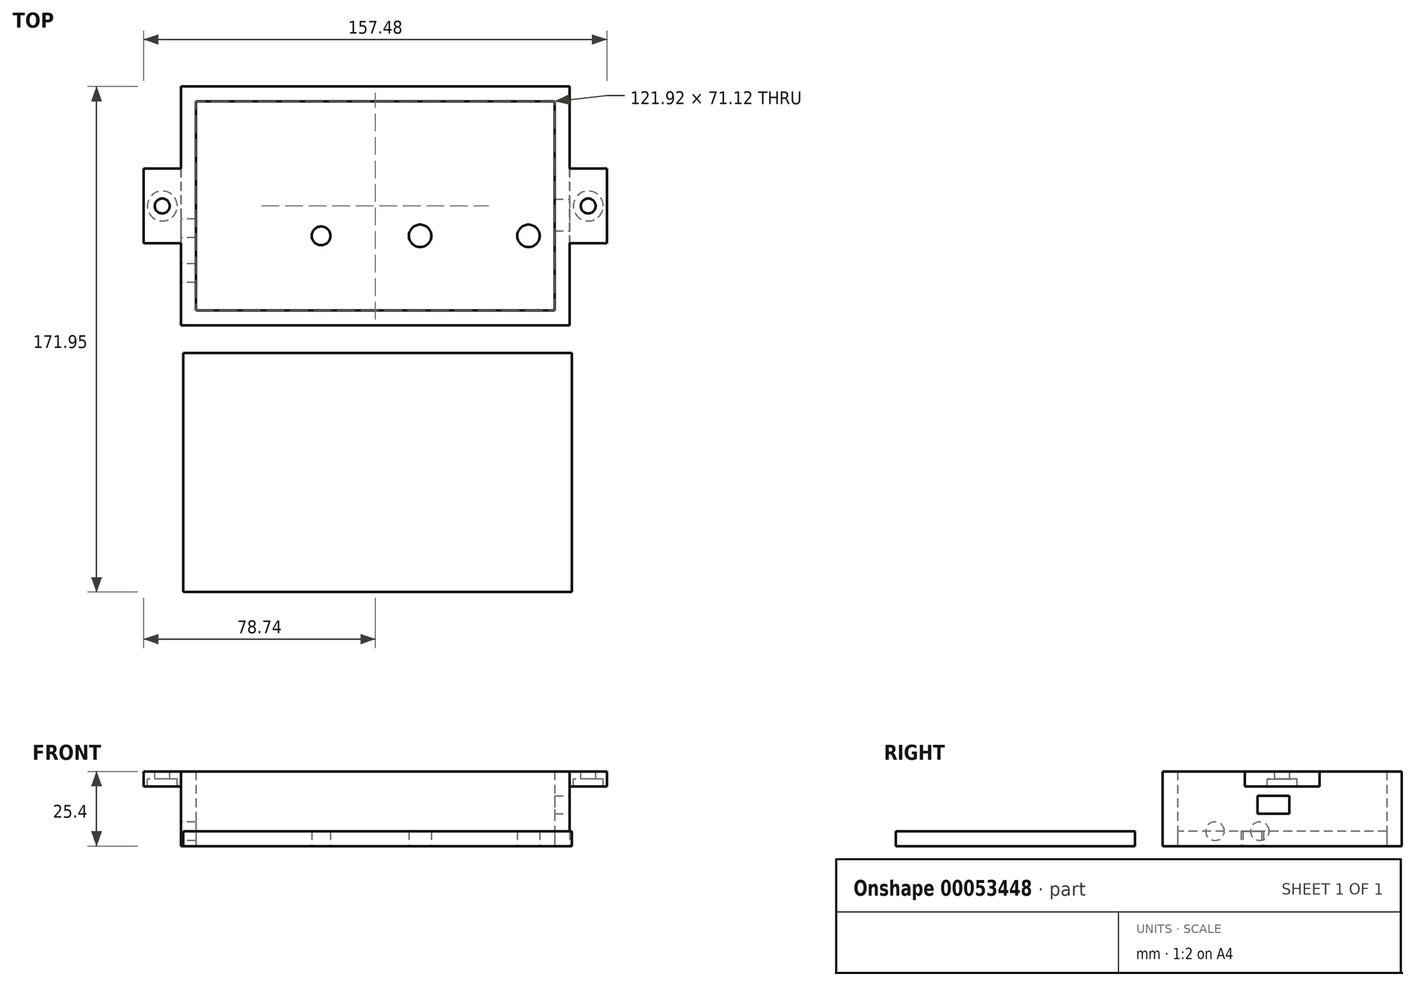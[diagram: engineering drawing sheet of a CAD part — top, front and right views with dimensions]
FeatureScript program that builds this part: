
annotation { "Feature Type Name" : "Feature", "Feature Type Description" : "" }
export const myFeature = defineFeature(function(context is Context, id is Id, definition is map)
    precondition{}
    {
        {
            var Q0;
            Q0=qCreatedBy(makeId("Top.planeOp"),FACE);
            var sketch = newSketch(context, id + "F0", { "sketchPlane" : qUnion([Q0])});
            skLineSegment(sketch, "E0.bottom", {"start": v(-121.92, 71.12) * mm, "end": v(0, 71.12) * mm});
            skLineSegment(sketch, "E0.top", {"start": v(-121.92, 0) * mm, "end": v(0, 0) * mm});
            skLineSegment(sketch, "E0.left", {"start": v(-121.92, 71.12) * mm, "end": v(-121.92, 0) * mm});
            skLineSegment(sketch, "E0.right", {"start": v(0, 71.12) * mm, "end": v(0, 0) * mm});
            skSolve(sketch);
        }
        {
            var Q0;
            Q0=makeQuery(id+"F0.imprint","IMPRINT",FACE,{"disambiguationData":[TD([[makeQuery(id+"F0.imprint","IMPRINT",EDGE,{"derivedFrom":sQuery(id+"F0.wireOp",EDGE,"E0.bottom")}),-1.0]])]});
            extrude(context, id + "F1", {"entities" : qUnion([Q0]), "depth" : 5.08 * mm});
        }
        {
            var Q0;
            Q0=makeQuery(id+"F1.opExtrude","CAP_FACE",FACE,{"disambiguationData":[OSD([sQuery(id+"F0.wireOp",EDGE,"E0.bottom"),sQuery(id+"F0.wireOp",EDGE,"E0.top"),sQuery(id+"F0.wireOp",EDGE,"E0.left"),sQuery(id+"F0.wireOp",EDGE,"E0.right")])],"isStart":true});
            var sketch = newSketch(context, id + "F2", { "sketchPlane" : qUnion([Q0])});
            skLineSegment(sketch, "E1.bottom", {"start": v(5.08, 5.08) * mm, "end": v(-127, 5.08) * mm});
            skLineSegment(sketch, "E1.top", {"start": v(5.08, -76.2) * mm, "end": v(-127, -76.2) * mm});
            skLineSegment(sketch, "E1.left", {"start": v(5.08, 5.08) * mm, "end": v(5.08, -76.2) * mm});
            skLineSegment(sketch, "E1.right", {"start": v(-127, 5.08) * mm, "end": v(-127, -76.2) * mm});
            skSolve(sketch);
        }
        {
            var Q0;
            {var subQ0=sQuery(id+"F2.wireOp",EDGE,"E1.top");Q0=makeQuery(id+"F2.imprint","IMPRINT",FACE,{"disambiguationData":[TD([[makeQuery(id+"F2.imprint","IMPRINT",EDGE,{"derivedFrom":subQ0}),-1.0]])]});}
            extrude(context, id + "F3", {"entities" : qUnion([Q0]), "oppositeDirection" : true, "depth" : 25.4 * mm});
        }
        {
            var Q0;
            Q0=makeQuery(id+"F1.opExtrude","CAP_FACE",FACE,{"disambiguationData":[OSD([sQuery(id+"F0.wireOp",EDGE,"E0.bottom"),sQuery(id+"F0.wireOp",EDGE,"E0.top"),sQuery(id+"F0.wireOp",EDGE,"E0.left"),sQuery(id+"F0.wireOp",EDGE,"E0.right")])],"isStart":true});
            var sketch = newSketch(context, id + "F4", { "sketchPlane" : qUnion([Q0])});
            skCircle(sketch, "E2", {"center": v(-45.72, -25.4) * mm, "radius": 3.8 * mm});
            skSolve(sketch);
        }
        {
            var Q0;
            Q0=makeQuery(id+"F4.imprint","IMPRINT",FACE,{"disambiguationData":[TD([[makeQuery(id+"F4.imprint","IMPRINT",EDGE,{"derivedFrom":sQuery(id+"F4.wireOp",EDGE,"E2")}),1.0]])]});
            extrude(context, id + "F5", {"entities" : qUnion([Q0]), "operationType" : NewBodyOperationType.REMOVE, "oppositeDirection" : true, "depth" : 5.08 * mm});
        }
        {
            var Q0;
            Q0=makeQuery(id+"F1.opExtrude","CAP_FACE",FACE,{"disambiguationData":[OSD([sQuery(id+"F0.wireOp",EDGE,"E0.bottom"),sQuery(id+"F0.wireOp",EDGE,"E0.top"),sQuery(id+"F0.wireOp",EDGE,"E0.left"),sQuery(id+"F0.wireOp",EDGE,"E0.right")])],"isStart":true});
            var sketch = newSketch(context, id + "F6", { "sketchPlane" : qUnion([Q0])});
            skCircle(sketch, "E3", {"center": v(-8.9, -25.4) * mm, "radius": 3.81 * mm});
            skSolve(sketch);
        }
        {
            var Q0;
            Q0=makeQuery(id+"F6.imprint","IMPRINT",FACE,{"disambiguationData":[TD([[makeQuery(id+"F6.imprint","IMPRINT",EDGE,{"derivedFrom":sQuery(id+"F6.wireOp",EDGE,"E3")}),1.0]])]});
            extrude(context, id + "F7", {"entities" : qUnion([Q0]), "operationType" : NewBodyOperationType.REMOVE, "oppositeDirection" : true, "depth" : 5.08 * mm});
        }
        {
            var Q0;
            Q0=makeQuery(id+"F1.opExtrude","CAP_FACE",FACE,{"disambiguationData":[OSD([sQuery(id+"F0.wireOp",EDGE,"E0.bottom"),sQuery(id+"F0.wireOp",EDGE,"E0.top"),sQuery(id+"F0.wireOp",EDGE,"E0.left"),sQuery(id+"F0.wireOp",EDGE,"E0.right")])],"isStart":true});
            var sketch = newSketch(context, id + "F8", { "sketchPlane" : qUnion([Q0])});
            skCircle(sketch, "E4", {"center": v(-79.38, -25.4) * mm, "radius": 3.18 * mm});
            skSolve(sketch);
        }
        {
            var Q0;
            Q0=makeQuery(id+"F8.imprint","IMPRINT",FACE,{"disambiguationData":[TD([[makeQuery(id+"F8.imprint","IMPRINT",EDGE,{"derivedFrom":sQuery(id+"F8.wireOp",EDGE,"E4")}),1.0]])]});
            extrude(context, id + "F9", {"entities" : qUnion([Q0]), "operationType" : NewBodyOperationType.REMOVE, "oppositeDirection" : true, "depth" : 5.08 * mm});
        }
        {
            var Q0;
            Q0=makeQuery(id+"F3.opExtrude","SWEPT_FACE",FACE,{"disambiguationData":[OSD([sQuery(id+"F2.wireOp",EDGE,"E1.right")])]});
            var sketch = newSketch(context, id + "F10", { "sketchPlane" : qUnion([Q0])});
            skCircle(sketch, "E5", {"center": v(-27.94, 5.08) * mm, "radius": 3.18 * mm});
            skSolve(sketch);
        }
        {
            var Q0;
            Q0=makeQuery(id+"F10.imprint","IMPRINT",FACE,{"disambiguationData":[TD([[makeQuery(id+"F10.imprint","IMPRINT",EDGE,{"derivedFrom":sQuery(id+"F10.wireOp",EDGE,"E5")}),-1.0]])]});
            var sketch = newSketch(context, id + "F11", { "sketchPlane" : qUnion([Q0])});
            skCircle(sketch, "E6", {"center": v(-12.7, 5.08) * mm, "radius": 3.18 * mm});
            skSolve(sketch);
        }
        {
            var Q0;
            Q0=makeQuery(id+"F11.imprint","IMPRINT",FACE,{"disambiguationData":[TD([[makeQuery(id+"F11.imprint","IMPRINT",EDGE,{"derivedFrom":makeQuery(id+"F10.imprint","IMPRINT",EDGE,{"derivedFrom":sQuery(id+"F10.wireOp",EDGE,"E5")})}),1.0]])]});
            extrude(context, id + "F12", {"entities" : qUnion([Q0]), "operationType" : NewBodyOperationType.REMOVE, "oppositeDirection" : true, "depth" : 5.08 * mm});
        }
        {
            var Q0;
            Q0 = qSketchRegion(id + "F11", true);
            extrude(context, id + "F13", {"entities" : qUnion([Q0]), "operationType" : NewBodyOperationType.REMOVE, "oppositeDirection" : true, "depth" : 5.08 * mm});
        }
        {
            var Q0;
            Q0=makeQuery(id+"F3.opExtrude","SWEPT_FACE",FACE,{"disambiguationData":[OSD([sQuery(id+"F2.wireOp",EDGE,"E1.left")])]});
            var sketch = newSketch(context, id + "F14", { "sketchPlane" : qUnion([Q0])});
            skLineSegment(sketch, "E7.bottom", {"start": v(37.94, 17.1) * mm, "end": v(27.12, 17.1) * mm});
            skLineSegment(sketch, "E7.top", {"start": v(37.94, 11) * mm, "end": v(27.12, 11) * mm});
            skLineSegment(sketch, "E7.left", {"start": v(37.94, 17.1) * mm, "end": v(37.94, 11) * mm});
            skLineSegment(sketch, "E7.right", {"start": v(27.12, 17.1) * mm, "end": v(27.12, 11) * mm});
            skSolve(sketch);
        }
        {
            var Q0;
            Q0 = qSketchRegion(id + "F14", true);
            extrude(context, id + "F15", {"entities" : qUnion([Q0]), "operationType" : NewBodyOperationType.REMOVE, "oppositeDirection" : true, "depth" : 5.08 * mm});
        }
        {
            var Q0;
            Q0=makeQuery(id+"F3.opExtrude","SWEPT_FACE",FACE,{"disambiguationData":[OSD([sQuery(id+"F2.wireOp",EDGE,"E1.left")])]});
            var sketch = newSketch(context, id + "F16", { "sketchPlane" : qUnion([Q0])});
            skLineSegment(sketch, "E8.bottom", {"start": v(48.26, 25.4) * mm, "end": v(22.86, 25.4) * mm});
            skLineSegment(sketch, "E8.top", {"start": v(48.26, 20.32) * mm, "end": v(22.86, 20.32) * mm});
            skLineSegment(sketch, "E8.left", {"start": v(48.26, 25.4) * mm, "end": v(48.26, 20.32) * mm});
            skLineSegment(sketch, "E8.right", {"start": v(22.86, 25.4) * mm, "end": v(22.86, 20.32) * mm});
            skSolve(sketch);
        }
        {
            var Q0;
            Q0=makeQuery(id+"F16.imprint","IMPRINT",FACE,{"disambiguationData":[TD([[makeQuery(id+"F16.imprint","IMPRINT",EDGE,{"derivedFrom":sQuery(id+"F16.wireOp",EDGE,"E8.bottom")}),-1.0]])]});
            extrude(context, id + "F17", {"entities" : qUnion([Q0]), "operationType" : NewBodyOperationType.ADD, "depth" : 12.7 * mm});
        }
        {
            var Q0;
            Q0=makeQuery(id+"F10.imprint","IMPRINT",FACE,{"disambiguationData":[TD([[makeQuery(id+"F10.imprint","IMPRINT",EDGE,{"derivedFrom":sQuery(id+"F10.wireOp",EDGE,"E5")}),-1.0]])]});
            var sketch = newSketch(context, id + "F18", { "sketchPlane" : qUnion([Q0])});
            skLineSegment(sketch, "E9.bottom", {"start": v(-48.26, 25.4) * mm, "end": v(-22.86, 25.4) * mm});
            skLineSegment(sketch, "E9.top", {"start": v(-48.26, 20.32) * mm, "end": v(-22.86, 20.32) * mm});
            skLineSegment(sketch, "E9.left", {"start": v(-48.26, 25.4) * mm, "end": v(-48.26, 20.32) * mm});
            skLineSegment(sketch, "E9.right", {"start": v(-22.86, 25.4) * mm, "end": v(-22.86, 20.32) * mm});
            skSolve(sketch);
        }
        {
            var Q0;
            Q0 = qSketchRegion(id + "F18", true);
            extrude(context, id + "F19", {"entities" : qUnion([Q0]), "operationType" : NewBodyOperationType.ADD, "depth" : 12.7 * mm});
        }
        {
            var Q0;
            Q0=makeQuery(id+"F19.boolean.opBoolean","MERGE",FACE,{"derivedFrom":[makeQuery(id+"F17.boolean.opBoolean","MERGE",FACE,{"derivedFrom":[makeQuery(id+"F3.opExtrude","CAP_FACE",FACE,{"disambiguationData":[OSD([sQuery(id+"F0.wireOp",EDGE,"E0.bottom"),sQuery(id+"F0.wireOp",EDGE,"E0.top"),sQuery(id+"F0.wireOp",EDGE,"E0.left"),sQuery(id+"F0.wireOp",EDGE,"E0.right"),sQuery(id+"F2.wireOp",EDGE,"E1.bottom"),sQuery(id+"F2.wireOp",EDGE,"E1.top"),sQuery(id+"F2.wireOp",EDGE,"E1.left"),sQuery(id+"F2.wireOp",EDGE,"E1.right")])],"isStart":false}),makeQuery(id+"F17.opExtrude","SWEPT_FACE",FACE,{"disambiguationData":[OSD([sQuery(id+"F16.wireOp",EDGE,"E8.bottom")])]})]}),makeQuery(id+"F19.opExtrude","SWEPT_FACE",FACE,{"disambiguationData":[OSD([sQuery(id+"F18.wireOp",EDGE,"E9.bottom")])]})]});
            var sketch = newSketch(context, id + "F20", { "sketchPlane" : qUnion([Q0])});
            skCircle(sketch, "E10", {"center": v(11.43, 35.56) * mm, "radius": 5.08 * mm});
            skSolve(sketch);
        }
        {
            var Q0;
            Q0 = qSketchRegion(id + "F20", true);
            extrude(context, id + "F21", {"entities" : qUnion([Q0]), "operationType" : NewBodyOperationType.REMOVE, "oppositeDirection" : true, "depth" : 5.08 * mm});
        }
        {
            var Q0;
            Q0=makeQuery(id+"F19.boolean.opBoolean","MERGE",FACE,{"derivedFrom":[makeQuery(id+"F17.boolean.opBoolean","MERGE",FACE,{"derivedFrom":[makeQuery(id+"F3.opExtrude","CAP_FACE",FACE,{"disambiguationData":[OSD([sQuery(id+"F0.wireOp",EDGE,"E0.bottom"),sQuery(id+"F0.wireOp",EDGE,"E0.top"),sQuery(id+"F0.wireOp",EDGE,"E0.left"),sQuery(id+"F0.wireOp",EDGE,"E0.right"),sQuery(id+"F2.wireOp",EDGE,"E1.bottom"),sQuery(id+"F2.wireOp",EDGE,"E1.top"),sQuery(id+"F2.wireOp",EDGE,"E1.left"),sQuery(id+"F2.wireOp",EDGE,"E1.right")])],"isStart":false}),makeQuery(id+"F17.opExtrude","SWEPT_FACE",FACE,{"disambiguationData":[OSD([sQuery(id+"F16.wireOp",EDGE,"E8.bottom")])]})]}),makeQuery(id+"F19.opExtrude","SWEPT_FACE",FACE,{"disambiguationData":[OSD([sQuery(id+"F18.wireOp",EDGE,"E9.bottom")])]})]});
            var sketch = newSketch(context, id + "F22", { "sketchPlane" : qUnion([Q0])});
            skCircle(sketch, "E11", {"center": v(-133.35, 35.56) * mm, "radius": 5.08 * mm});
            skSolve(sketch);
        }
        {
            var Q0;
            Q0 = qSketchRegion(id + "F22", true);
            extrude(context, id + "F23", {"entities" : qUnion([Q0]), "operationType" : NewBodyOperationType.REMOVE, "oppositeDirection" : true, "depth" : 5.08 * mm});
        }
        {
            var Q0;
            Q0=qCreatedBy(makeId("Top.planeOp"),FACE);
            var sketch = newSketch(context, id + "F24", { "sketchPlane" : qUnion([Q0])});
            skLineSegment(sketch, "E12.bottom", {"start": v(5.86, -14.47) * mm, "end": v(-126.22, -14.47) * mm});
            skLineSegment(sketch, "E12.top", {"start": v(5.86, -95.75) * mm, "end": v(-126.22, -95.75) * mm});
            skLineSegment(sketch, "E12.left", {"start": v(5.86, -14.47) * mm, "end": v(5.86, -95.75) * mm});
            skLineSegment(sketch, "E12.right", {"start": v(-126.22, -14.47) * mm, "end": v(-126.22, -95.75) * mm});
            skSolve(sketch);
        }
        {
            var Q0;
            Q0=makeQuery(id+"F24.imprint","IMPRINT",FACE,{"disambiguationData":[TD([[makeQuery(id+"F24.imprint","IMPRINT",EDGE,{"derivedFrom":sQuery(id+"F24.wireOp",EDGE,"E12.bottom")}),1.0]])]});
            extrude(context, id + "F25", {"entities" : qUnion([Q0]), "depth" : 5.08 * mm});
        }
        {
            var Q0;
            Q0=makeQuery(id+"F19.boolean.opBoolean","MERGE",FACE,{"derivedFrom":[makeQuery(id+"F17.boolean.opBoolean","MERGE",FACE,{"derivedFrom":[makeQuery(id+"F3.opExtrude","CAP_FACE",FACE,{"disambiguationData":[OSD([sQuery(id+"F0.wireOp",EDGE,"E0.bottom"),sQuery(id+"F0.wireOp",EDGE,"E0.top"),sQuery(id+"F0.wireOp",EDGE,"E0.left"),sQuery(id+"F0.wireOp",EDGE,"E0.right"),sQuery(id+"F2.wireOp",EDGE,"E1.bottom"),sQuery(id+"F2.wireOp",EDGE,"E1.top"),sQuery(id+"F2.wireOp",EDGE,"E1.left"),sQuery(id+"F2.wireOp",EDGE,"E1.right")])],"isStart":false}),makeQuery(id+"F17.opExtrude","SWEPT_FACE",FACE,{"disambiguationData":[OSD([sQuery(id+"F16.wireOp",EDGE,"E8.bottom")])]})]}),makeQuery(id+"F19.opExtrude","SWEPT_FACE",FACE,{"disambiguationData":[OSD([sQuery(id+"F18.wireOp",EDGE,"E9.bottom")])]})]});
            var sketch = newSketch(context, id + "F26", { "sketchPlane" : qUnion([Q0])});
            skCircle(sketch, "E13.0", {"center": v(11.43, 35.56) * mm, "radius": 5.08 * mm});
            skLineSegment(sketch, "E14", {"start": v(11.43, 35.56) * mm, "end": v(8.9, 35.56) * mm});
            skLineSegment(sketch, "E15", {"start": v(8.9, 35.56) * mm, "end": v(6.35, 35.56) * mm});
            skCircle(sketch, "E16", {"center": v(11.43, 35.56) * mm, "radius": 2.54 * mm});
            skLineSegment(sketch, "E17.1", {"start": v(5.08, -5.08) * mm, "end": v(-127, -5.08) * mm});
            skLineSegment(sketch, "E18", {"start": v(-60.96, -5.08) * mm, "end": v(-60.96, 76.2) * mm, "construction": true});
            skCircle(sketch, "E19.MirrorC", {"center": v(-133.35, 35.56) * mm, "radius": 5.08 * mm});
            skCircle(sketch, "E20.MirrorC", {"center": v(-133.35, 35.56) * mm, "radius": 2.54 * mm});
            skSolve(sketch);
        }
        {
            var Q0;
            Q0=makeQuery(id+"F26.imprint","IMPRINT",FACE,{"disambiguationData":[TD([[makeQuery(id+"F26.imprint","IMPRINT",EDGE,{"derivedFrom":sQuery(id+"F26.wireOp",EDGE,"E13.0")}),1.0]])]});
            var Q1;
            Q1=makeQuery(id+"F26.imprint","IMPRINT",FACE,{"disambiguationData":[TD([[makeQuery(id+"F26.imprint","IMPRINT",EDGE,{"derivedFrom":sQuery(id+"F26.wireOp",EDGE,"E19.MirrorC")}),1.0]])]});
            extrude(context, id + "F27", {"entities" : qUnion([Q0, Q1]), "operationType" : NewBodyOperationType.ADD, "oppositeDirection" : true, "depth" : 2.54 * mm});
        }
    });
